# Revit family: ABRFB1480xxWSxxxMRM08xx
name_source: partatom
category: Leuchten
units: mm (PartAtom-declared; Revit-internal decimal feet)

## family parameters
Basisbauteil = Fläche
Beim Laden mit Abzugskörper schneiden = Nein
Bemaßung runder Anschluss = Durchmesser verwenden
Gemeinsam genutzt = Nein
Lichtquelle = Ja
OmniClass-Nummer = 23.80.70.11
OmniClass-Titel = Luminaries for Internal Lighting
Raumberechnungspunkt = Nein
Teiletyp = Normal

## types (4) — shared parameters
Baugruppenkennzeichen = D5020200
Datei für fotometrisches Netz = ABRFB_MRM.IES
Emissionsform beim Rendern sichtbar = Nein
Farbfilter = 16777215
Farbtemperaturverschiebung bei Dämpfen der Lampe = <Keine Auswahl>
Hersteller = RIDI Leuchten GmbH
Lampe = LED
Neigungswinkel = 90.00°
Scheinlast = 67 VA
URL = www.ridi.de
Von Breite des Rechtecks ausssenden = 1460 mm  [stored 4.79003 ft]
Von Länge des Rechtecks aussenden = 48 mm  [stored 0.15748 ft]
brand = RIDI
conformity mark = CE
electrical safety class = 1
height = 59 mm
ingress protection (IP) code = IP20
length = 1480 mm  [stored 4.85564 ft]
nominal frequency = 50-60Hz
nominal voltage = 230
rated input power = 67
voltage type (AC, DC, UC) = AC
weight = 4,22
width = 131 mm  [stored 0.42979 ft]
zero-valued in all types: Vorgabe-Ansicht

## per-type parameters (varying)
| type | Modell | product name |
| ABRFB1480DAWS830MRM0800 | 0667750 | ABRFB1480DAWS830MRM0800 |
| ABRFB1480DAWS840MRM0850 | 0667747 | ABRFB1480DAWS840MRM0850 |
| ABRFB1480NDWS830MRM0800 | 0657750 | ABRFB1480NDWS830MRM0800 |
| ABRFB1480NDWS840MRM0850 | 0657747 | ABRFB1480NDWS830MRM0800 |

note: [stored X ft] marks values corroborated as IEEE doubles in the binary element streams (Revit-internal decimal feet)
